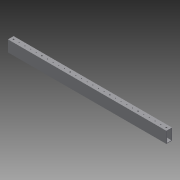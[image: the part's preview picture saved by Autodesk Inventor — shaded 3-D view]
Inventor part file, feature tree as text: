
AUTODESK INVENTOR PART (.ipt)
format: ipt  version: 2015 SP1 (Build 190203100, 203)  size: 226,816 bytes
history: native  units: in
note: dims shown in document units (in); Inventor stores cm internally (conversion verified against a paired STEP export)
features: sketch x4, projected_geometry x3, extrude x2, hole x2, pattern_linear x1
ambient origin geometry x8: Origin, YZ Plane, XZ Plane, XY Plane, X Axis, Y Axis, Z Axis, Center Point
bodies: Solid1 (feature_tree)
feature tree (12):
  extrude  "Extrusion1"  Depth=1.0in
  hole  "Hole1"  [1 undecoded]
  pattern_linear  "Rectangular Pattern1"  Spacing1=28.0in  [1 undecoded]
  extrude  "Extrusion4"  Depth=1.0in
  hole  "Hole3"  [1 undecoded]
  sketch  "Sketch1"  dims[d0=2.0in d1=1.0in]
  sketch  "Sketch2"  dims[d2=1.8in d3=0.8in]
  projected_geometry  "Projected Loop1"
  sketch  "Sketch6"  dims[d4=0.1in]
  projected_geometry  "Projected Loop5"
  sketch  "Sketch7"  dims[d5=0.1in d6=28.0in d7=0.0in d9=0.5in d10=0.5in d11=0.1562in d12=0.75in d13=0.375in d14=0.25in d15=0.5635in d16=1.0in d17=0.8108in d18=11.0236in d20=1.0in d58=0.25in d59=0.25in d60=0.25in d61=0.25in d62=0.25in d63=0.25in d64=2.0in d65=0.0in d66=0.5in d67=0.5in d68=0.5in d69=0.5in d70=2.0in d71=3.0in d72=4.0in d73=5.0in d74=2.0in d75=3.0in d76=4.0in d77=5.0in d78=0.5in d79=0.5in d80=0.5in d81=0.5in d82=0.1562in d83=0.75in d84=0.375in d85=0.25in d86=0.5635in d87=1.0in d88=0.8108in]
  projected_geometry  "Projected Loop6"
note: 3 required parameter values undecoded (feature->parameter linkage not recoverable at this tier; creation-order binding heuristic only, values carry confidence <= 0.55)
